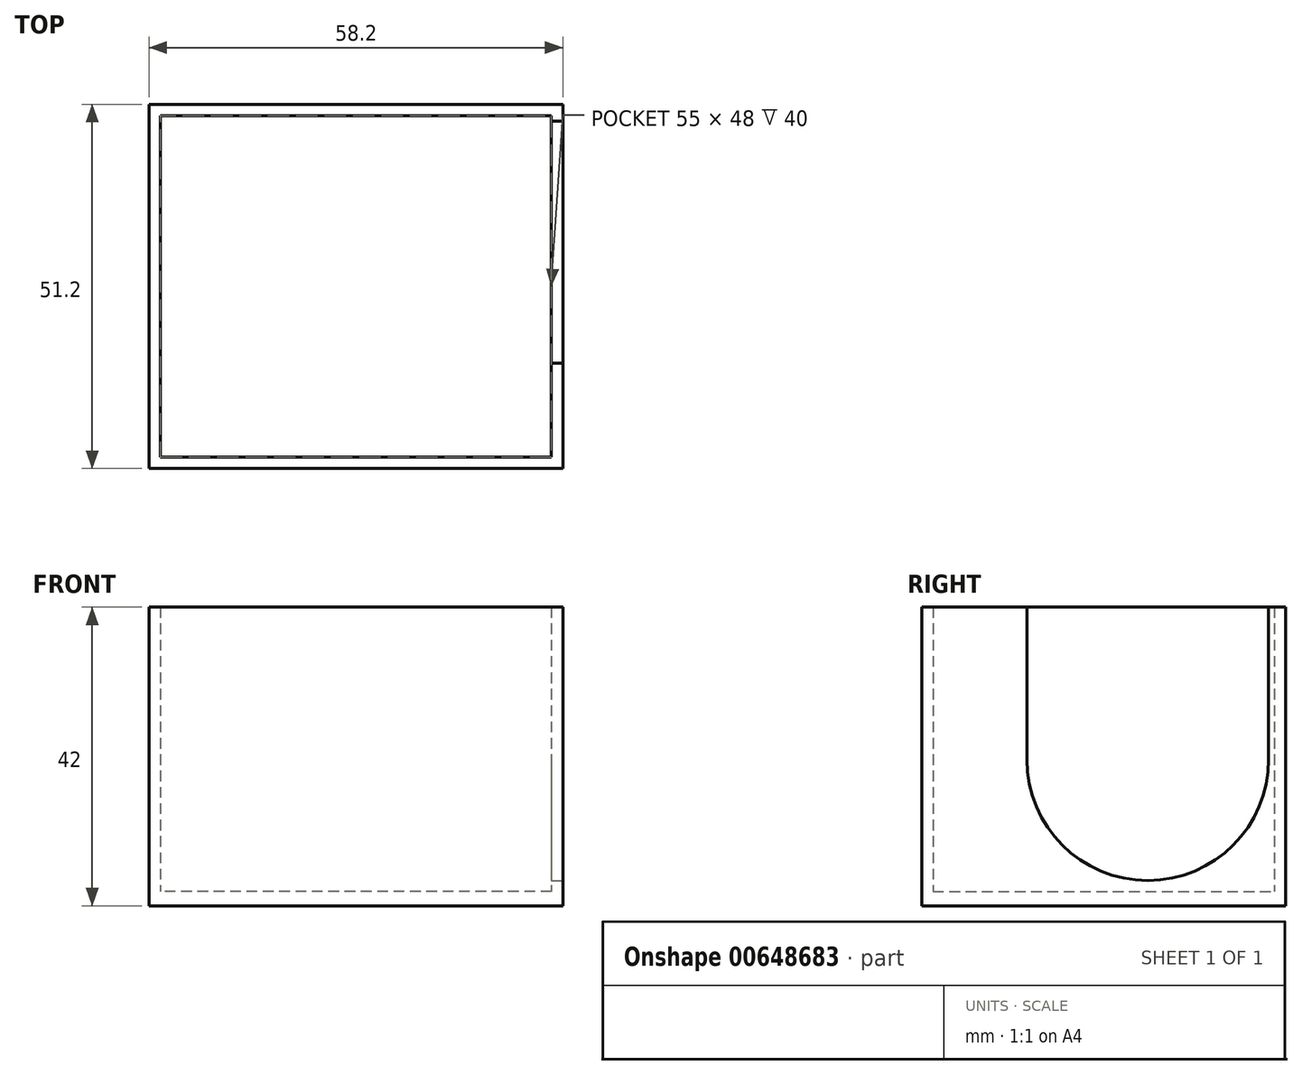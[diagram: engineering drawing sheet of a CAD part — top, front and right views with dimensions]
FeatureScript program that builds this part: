
annotation { "Feature Type Name" : "Feature", "Feature Type Description" : "" }
export const myFeature = defineFeature(function(context is Context, id is Id, definition is map)
    precondition{}
    {
        {
            var Q0;
            Q0=qCreatedBy(makeId("Top.planeOp"),FACE);
            var sketch = newSketch(context, id + "F0", { "sketchPlane" : qUnion([Q0])});
            skLineSegment(sketch, "E0.bottom", {"start": v(27.5, -24) * mm, "end": v(-27.5, -24) * mm});
            skLineSegment(sketch, "E0.top", {"start": v(27.5, 24) * mm, "end": v(-27.5, 24) * mm});
            skLineSegment(sketch, "E0.left", {"start": v(27.5, -24) * mm, "end": v(27.5, 24) * mm});
            skLineSegment(sketch, "E0.right", {"start": v(-27.5, -24) * mm, "end": v(-27.5, 24) * mm});
            skPoint(sketch, "E0.middle", {"position": v(0, 0) * mm});
            skLineSegment(sketch, "E1.0", {"start": v(29.1, 25.6) * mm, "end": v(-29.1, 25.6) * mm});
            skLineSegment(sketch, "E1.1", {"start": v(29.1, -25.6) * mm, "end": v(29.1, 25.6) * mm});
            skLineSegment(sketch, "E1.2", {"start": v(29.1, -25.6) * mm, "end": v(-29.1, -25.6) * mm});
            skLineSegment(sketch, "E1.3", {"start": v(-29.1, -25.6) * mm, "end": v(-29.1, 25.6) * mm});
            skSolve(sketch);
        }
        {
            var Q0;
            Q0=makeQuery(id+"F0.imprint","IMPRINT",FACE,{"disambiguationData":[TD([[makeQuery(id+"F0.imprint","IMPRINT",EDGE,{"derivedFrom":sQuery(id+"F0.wireOp",EDGE,"E0.bottom")}),-1.0]])]});
            extrude(context, id + "F1", {"entities" : qUnion([Q0]), "depth" : 2 * mm, "offsetDistance" : 25 * mm});
        }
        {
            var Q0;
            Q0=makeQuery(id+"F0.imprint","IMPRINT",FACE,{"disambiguationData":[TD([[makeQuery(id+"F0.imprint","IMPRINT",EDGE,{"derivedFrom":sQuery(id+"F0.wireOp",EDGE,"E0.bottom")}),1.0]])]});
            extrude(context, id + "F2", {"entities" : qUnion([Q0]), "operationType" : NewBodyOperationType.ADD, "depth" : 42 * mm, "offsetDistance" : 25 * mm});
        }
        {
            var Q0;
            Q0=makeQuery(id+"F2.opExtrude","SWEPT_FACE",FACE,{"disambiguationData":[OSD([sQuery(id+"F0.wireOp",EDGE,"E1.1")])]});
            var sketch = newSketch(context, id + "F3", { "sketchPlane" : qUnion([Q0])});
            skCircle(sketch, "E2", {"center": v(6.22, 20.55) * mm, "radius": 17 * mm});
            skLineSegment(sketch, "E3", {"start": v(23.22, 20.55) * mm, "end": v(23.22, 42) * mm});
            skLineSegment(sketch, "E4", {"start": v(-10.78, 20.55) * mm, "end": v(-10.78, 42) * mm});
            skSolve(sketch);
        }
        {
            var Q0;
            {var subQ0=sQuery(id+"F3.wireOp",EDGE,"E3");Q0=makeQuery(id+"F3.imprint","IMPRINT",FACE,{"disambiguationData":[TD([[makeQuery(id+"F3.imprint","IMPRINT",EDGE,{"derivedFrom":subQ0}),1.0]])]});}
            var Q1;
            {var subQ0=sQuery(id+"F3.wireOp",EDGE,"E2");var subQ1=makeQuery(id+"F3.imprint","INTERSECT",VERTEX,{"derivedFrom":[subQ0,sQuery(id+"F3.wireOp",EDGE,"E3")]});Q1=makeQuery(id+"F3.imprint","IMPRINT",FACE,{"disambiguationData":[TD([[makeQuery(id+"F3.imprint","IMPRINT",EDGE,{"disambiguationData":[TD([[subQ1,-1.0]])],"derivedFrom":subQ0}),1.0]])]});}
            extrude(context, id + "F4", {"entities" : qUnion([Q0, Q1]), "operationType" : NewBodyOperationType.REMOVE, "oppositeDirection" : true, "depth" : 4 * mm, "offsetDistance" : 25 * mm});
        }
    });
